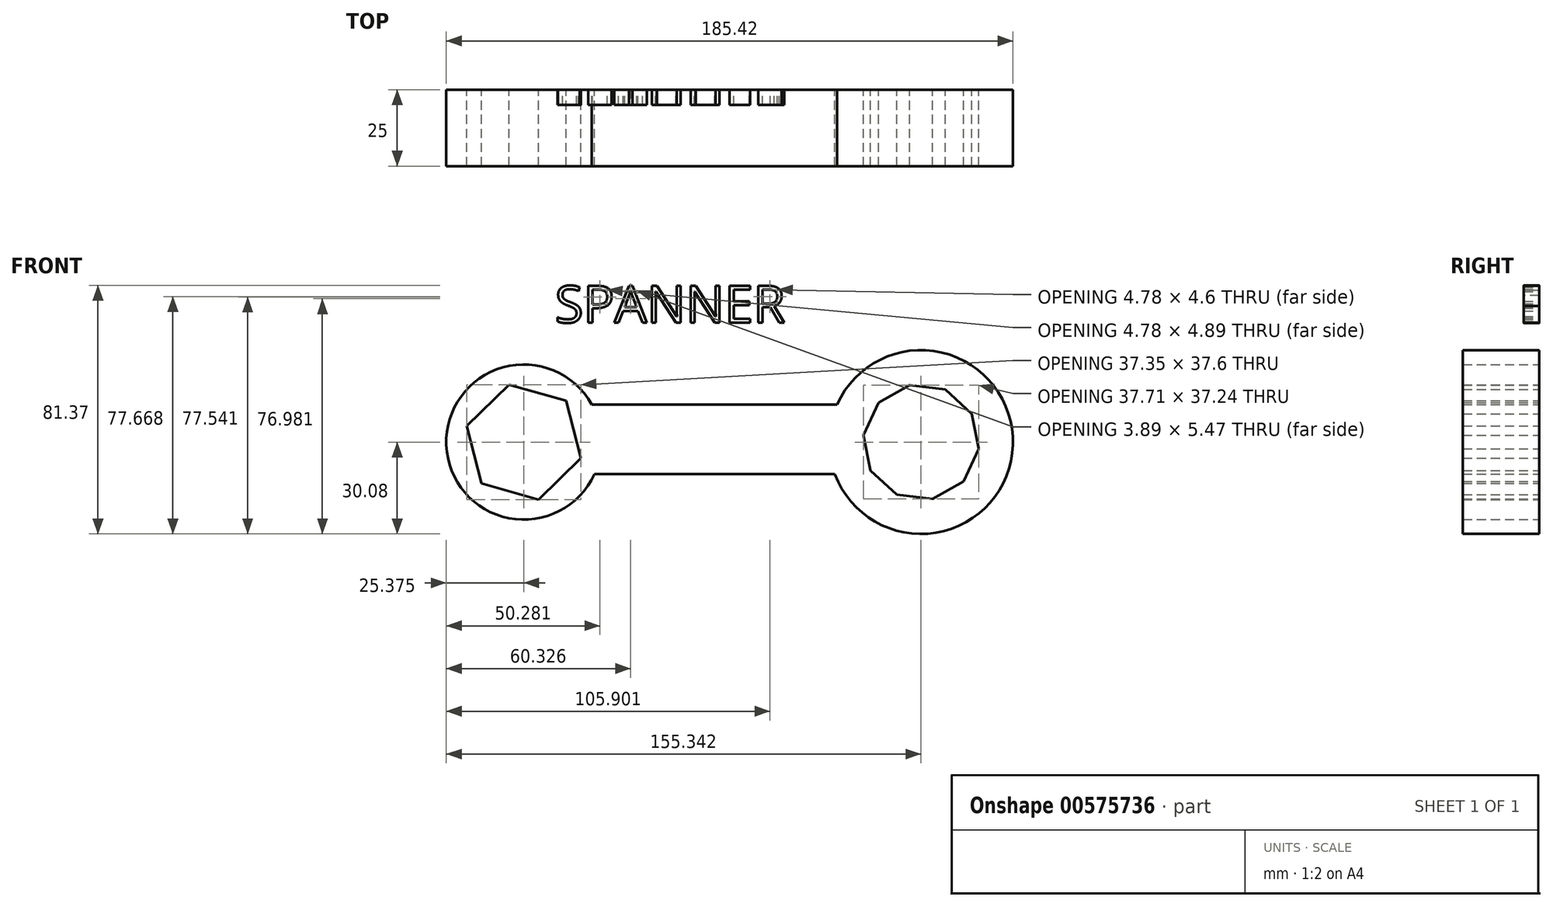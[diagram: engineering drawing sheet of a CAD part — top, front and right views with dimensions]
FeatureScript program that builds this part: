
annotation { "Feature Type Name" : "Feature", "Feature Type Description" : "" }
export const myFeature = defineFeature(function(context is Context, id is Id, definition is map)
    precondition{}
    {
        {
            var Q0;
            Q0=qCreatedBy(makeId("Front.planeOp"),FACE);
            var sketch = newSketch(context, id + "F0", { "sketchPlane" : qUnion([Q0])});
            skCircle(sketch, "E0", {"center": v(-74.6, 0) * mm, "radius": 25.37 * mm});
            skCircle(sketch, "E1", {"center": v(55.36, 0) * mm, "radius": 30.08 * mm});
            skLineSegment(sketch, "E2", {"start": v(-52.4, 12.28) * mm, "end": v(27.9, 12.28) * mm});
            skLineSegment(sketch, "E3", {"start": v(-51.51, -10.5) * mm, "end": v(27.18, -10.5) * mm});
            skCircle(sketch, "E4.cCircle", {"center": v(-74.6, 0) * mm, "radius": 16.8 * mm, "construction": true});
            skLineSegment(sketch, "E4.0", {"start": v(-60.72, 13.55) * mm, "end": v(-55.93, -5.26) * mm});
            skLineSegment(sketch, "E4.1", {"start": v(-55.93, -5.26) * mm, "end": v(-69.82, -18.8) * mm});
            skLineSegment(sketch, "E4.2", {"start": v(-69.82, -18.8) * mm, "end": v(-88.5, -13.55) * mm});
            skLineSegment(sketch, "E4.3", {"start": v(-88.5, -13.55) * mm, "end": v(-93.28, 5.26) * mm});
            skLineSegment(sketch, "E4.4", {"start": v(-93.28, 5.26) * mm, "end": v(-79.4, 18.8) * mm});
            skLineSegment(sketch, "E4.5", {"start": v(-79.4, 18.8) * mm, "end": v(-60.72, 13.55) * mm});
            skPoint(sketch, "E4.0.midPoint", {"position": v(-58.32, 4.14) * mm});
            skCircle(sketch, "E5.cCircle", {"center": v(55.36, 0) * mm, "radius": 18.06 * mm, "construction": true});
            skLineSegment(sketch, "E5.0", {"start": v(71.92, 9.28) * mm, "end": v(74.22, -2.23) * mm});
            skLineSegment(sketch, "E5.1", {"start": v(74.22, -2.23) * mm, "end": v(69.3, -12.89) * mm});
            skLineSegment(sketch, "E5.2", {"start": v(69.3, -12.89) * mm, "end": v(59.07, -18.62) * mm});
            skLineSegment(sketch, "E5.3", {"start": v(59.07, -18.62) * mm, "end": v(47.42, -17.24) * mm});
            skLineSegment(sketch, "E5.4", {"start": v(47.42, -17.24) * mm, "end": v(38.8, -9.28) * mm});
            skLineSegment(sketch, "E5.5", {"start": v(38.8, -9.28) * mm, "end": v(36.5, 2.23) * mm});
            skLineSegment(sketch, "E5.6", {"start": v(36.5, 2.23) * mm, "end": v(41.42, 12.89) * mm});
            skLineSegment(sketch, "E5.7", {"start": v(41.42, 12.89) * mm, "end": v(51.66, 18.62) * mm});
            skLineSegment(sketch, "E5.8", {"start": v(51.66, 18.62) * mm, "end": v(63.3, 17.24) * mm});
            skLineSegment(sketch, "E5.9", {"start": v(63.3, 17.24) * mm, "end": v(71.92, 9.28) * mm});
            skPoint(sketch, "E5.0.midPoint", {"position": v(73.07, 3.52) * mm});
            skSolve(sketch);
        }
        {
            var Q0;
            Q0 = qSketchRegion(id + "F0", true);
            extrude(context, id + "F1", {"entities" : qUnion([Q0]), "depth" : 25 * mm, "offsetDistance" : 25 * mm});
        }
        {
            var Q0;
            Q0=qCreatedBy(makeId("Front.planeOp"),FACE);
            var sketch = newSketch(context, id + "F2", { "sketchPlane" : qUnion([Q0])});
            skText(sketch, "E6", { "text": "SPANNER", "fontName": "OpenSans-Regular.ttf"});
            const initialGuessF2  = {"E6": [-0.0644, 0.03908, 1, 0, 0.01214]};
            skSetInitialGuess(sketch, initialGuessF2);
            skSolve(sketch);
        }
        {
            var Q0;
            Q0 = qSketchRegion(id + "F2", true);
            extrude(context, id + "F3", {"entities" : qUnion([Q0]), "depth" : 5 * mm, "offsetDistance" : 25 * mm});
        }
    });
